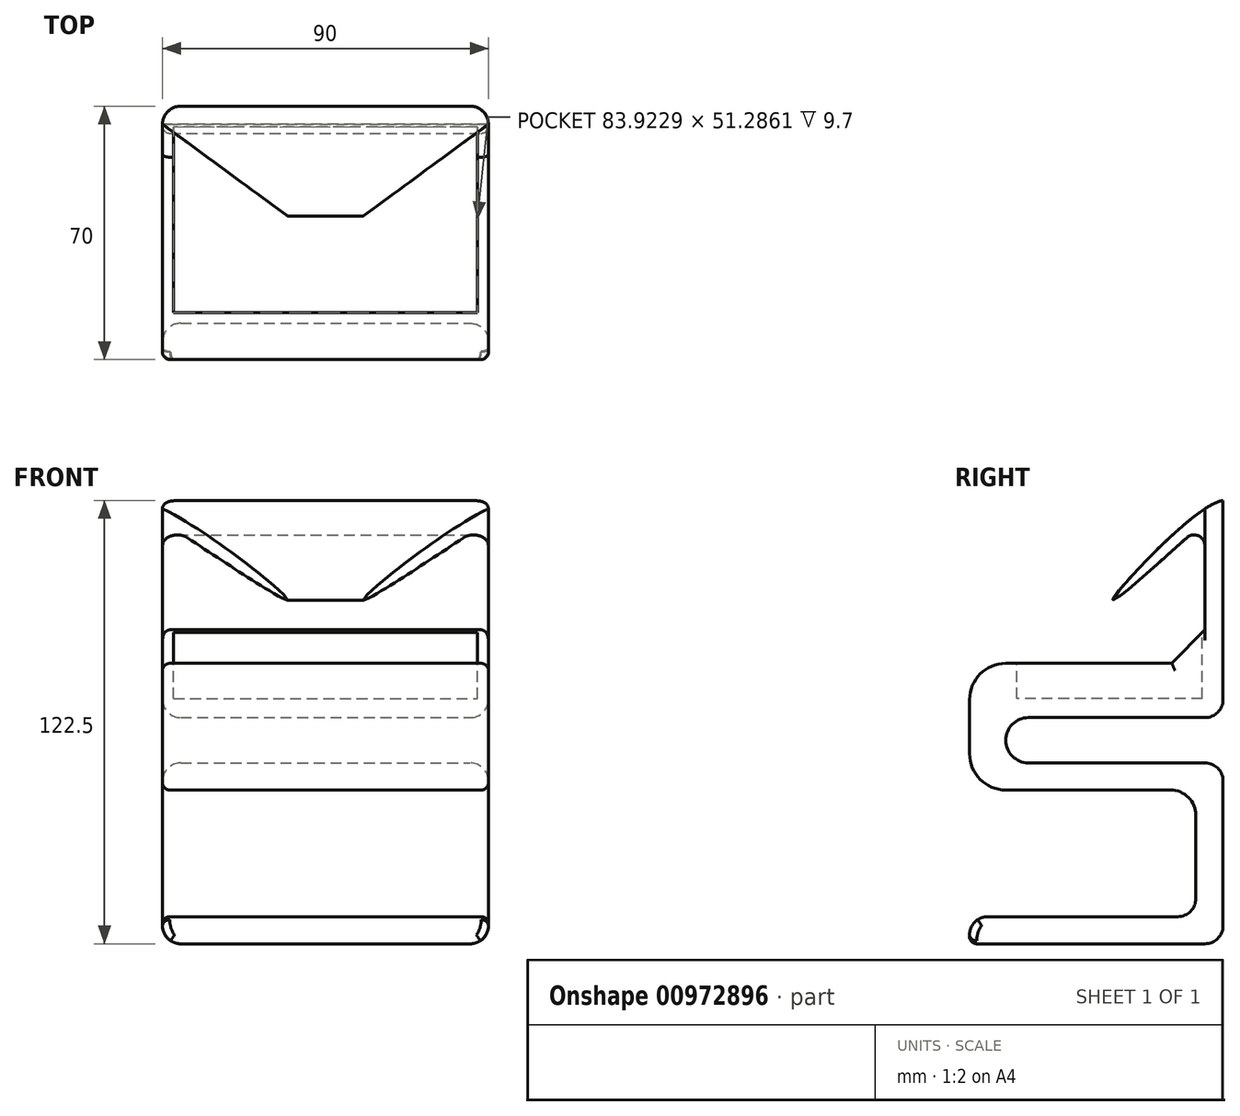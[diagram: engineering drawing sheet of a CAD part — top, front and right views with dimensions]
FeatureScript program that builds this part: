
annotation { "Feature Type Name" : "Feature", "Feature Type Description" : "" }
export const myFeature = defineFeature(function(context is Context, id is Id, definition is map)
    precondition{}
    {
        {
            var Q0;
            Q0=qCreatedBy(makeId("Right.planeOp"),FACE);
            var sketch = newSketch(context, id + "F0", { "sketchPlane" : qUnion([Q0])});
            skLineSegment(sketch, "E0", {"start": v(-39.75, -50) * mm, "end": v(30.25, -50) * mm});
            skLineSegment(sketch, "E1", {"start": v(-39.75, -50) * mm, "end": v(-39.75, -42.5) * mm});
            skLineSegment(sketch, "E2", {"start": v(-39.75, -42.5) * mm, "end": v(22.75, -42.5) * mm});
            skLineSegment(sketch, "E3", {"start": v(30.25, -50) * mm, "end": v(30.25, 0) * mm});
            skLineSegment(sketch, "E4", {"start": v(22.75, -42.5) * mm, "end": v(22.75, -7.5) * mm});
            skLineSegment(sketch, "E5", {"start": v(22.75, -7.5) * mm, "end": v(-39.75, -7.5) * mm});
            skLineSegment(sketch, "E6", {"start": v(-39.75, -7.5) * mm, "end": v(-39.75, 27.5) * mm});
            skLineSegment(sketch, "E7", {"start": v(30.25, 0) * mm, "end": v(-23.5, 0) * mm});
            skArc(sketch, "E8", {"start": v(-23.5, 12.5) * mm, "mid": v(-29.75, 6.25) * mm, "end": v(-23.5, 0) * mm});
            skLineSegment(sketch, "E9", {"start": v(-23.5, 12.5) * mm, "end": v(30.25, 12.5) * mm});
            skLineSegment(sketch, "E10", {"start": v(30.25, 12.5) * mm, "end": v(30.25, 72.5) * mm});
            skLineSegment(sketch, "E11", {"start": v(-39.75, 27.5) * mm, "end": v(16.15, 27.5) * mm});
            skLineSegment(sketch, "E12", {"start": v(16.15, 27.5) * mm, "end": v(25.25, 36.78) * mm});
            skLineSegment(sketch, "E13", {"start": v(25.25, 36.78) * mm, "end": v(25.25, 66.78) * mm});
            skFitSpline(sketch, "E14", {"points": [v(25.25, 66.78) * mm, v(0, 45.52) * mm, v(30.25, 72.5) * mm, v(32.32, 54.21) * mm], "startDerivative": vector(-115.72, -104.64) * mm, "endDerivative": vector(-15.53, -107.77) * mm});
            skSolve(sketch);
        }
        {
            var Q0;
            Q0=makeQuery(id+"F0.imprint","IMPRINT",FACE,{"disambiguationData":[TD([[makeQuery(id+"F0.imprint","IMPRINT",EDGE,{"derivedFrom":sQuery(id+"F0.wireOp",EDGE,"E0")}),1.0]])]});
            extrude(context, id + "F1", {"entities" : qUnion([Q0]), "oppositeDirection" : true, "depth" : 45 * mm, "offsetDistance" : 25 * mm, "hasSecondDirection" : true, "secondDirectionOppositeDirection" : false, "secondDirectionDepth" : 45 * mm});
        }
        {
            var Q0;
            Q0=makeQuery(id+"F1.opExtrude","SWEPT_EDGE",EDGE,{"disambiguationData":[OSD([sQuery(id+"F0.wireOp",EDGE,"E2"),sQuery(id+"F0.wireOp",EDGE,"E4")])]});
            var Q1;
            Q1=makeQuery(id+"F1.opExtrude","SWEPT_EDGE",EDGE,{"disambiguationData":[OSD([sQuery(id+"F0.wireOp",EDGE,"E1"),sQuery(id+"F0.wireOp",EDGE,"E2")])]});
            var Q2;
            Q2=makeQuery(id+"F1.opExtrude","SWEPT_EDGE",EDGE,{"disambiguationData":[OSD([sQuery(id+"F0.wireOp",EDGE,"E3"),sQuery(id+"F0.wireOp",EDGE,"E7")])]});
            var Q3;
            Q3=makeQuery(id+"F1.opExtrude","SWEPT_EDGE",EDGE,{"disambiguationData":[OSD([sQuery(id+"F0.wireOp",EDGE,"E9"),sQuery(id+"F0.wireOp",EDGE,"E10")])]});
            var Q4;
            Q4=makeQuery(id+"F1.opExtrude","SWEPT_EDGE",EDGE,{"disambiguationData":[OSD([sQuery(id+"F0.wireOp",EDGE,"E0"),sQuery(id+"F0.wireOp",EDGE,"E3")])]});
            fillet(context, id + "F2", {"entities" : qUnion([Q0, Q1, Q2, Q3, Q4]), "radius" : 5 * mm, "tangentPropagation" : true, "allowEdgeOverflow" : false});
        }
        {
            var Q0;
            Q0=makeQuery(id+"F1.opExtrude","SWEPT_EDGE",EDGE,{"disambiguationData":[OSD([sQuery(id+"F0.wireOp",EDGE,"E6"),sQuery(id+"F0.wireOp",EDGE,"E11")])]});
            var Q1;
            Q1=makeQuery(id+"F1.opExtrude","SWEPT_EDGE",EDGE,{"disambiguationData":[OSD([sQuery(id+"F0.wireOp",EDGE,"E5"),sQuery(id+"F0.wireOp",EDGE,"E6")])]});
            fillet(context, id + "F3", {"entities" : qUnion([Q0, Q1]), "radius" : 10 * mm, "tangentPropagation" : true, "allowEdgeOverflow" : false});
        }
        {
            var Q0;
            Q0=makeQuery(id+"F1.opExtrude","SWEPT_EDGE",EDGE,{"disambiguationData":[OSD([sQuery(id+"F0.wireOp",EDGE,"E4"),sQuery(id+"F0.wireOp",EDGE,"E5")])]});
            fillet(context, id + "F4", {"entities" : qUnion([Q0]), "radius" : 7 * mm, "tangentPropagation" : true, "allowEdgeOverflow" : false});
        }
        {
            var Q0;
            Q0=qCreatedBy(makeId("Top.planeOp"),FACE);
            cPlane(context, id + "F5", {"entities" : qUnion([Q0]), "cplaneType" : CPlaneType.OFFSET, "offset" : 72.7 * mm, "width" : 150 * mm, "height" : 150 * mm});
        }
        {
            var Q0;
            Q0=qCreatedBy(id+"F5.planeOp",FACE);
            var sketch = newSketch(context, id + "F6", { "sketchPlane" : qUnion([Q0])});
            skLineSegment(sketch, "E15", {"start": v(0, 0) * mm, "end": v(0, 30.25) * mm});
            skLineSegment(sketch, "E16", {"start": v(0, 30.25) * mm, "end": v(-45, 30.25) * mm});
            skLineSegment(sketch, "E17", {"start": v(-45, 30.25) * mm, "end": v(-45, 25.25) * mm});
            skLineSegment(sketch, "E18", {"start": v(0.72, 30.25) * mm, "end": v(45, 30.25) * mm});
            skLineSegment(sketch, "E19", {"start": v(45, 30.25) * mm, "end": v(45, 25.25) * mm});
            skLineSegment(sketch, "E20", {"start": v(0, -0.44) * mm, "end": v(-10, -0.44) * mm});
            skLineSegment(sketch, "E21", {"start": v(-45, 25.25) * mm, "end": v(-10, -0.44) * mm});
            skLineSegment(sketch, "E22", {"start": v(-10, -0.44) * mm, "end": v(-45.04, -0.44) * mm});
            skLineSegment(sketch, "E23", {"start": v(-45, 25.25) * mm, "end": v(-45.04, -0.44) * mm});
            skLineSegment(sketch, "E24.MirrorCS", {"start": v(45, 25.25) * mm, "end": v(45.04, -0.44) * mm});
            skLineSegment(sketch, "E25.MirrorCS", {"start": v(10, -0.44) * mm, "end": v(45.04, -0.44) * mm});
            skLineSegment(sketch, "E26.MirrorCS", {"start": v(45, 25.25) * mm, "end": v(10, -0.44) * mm});
            skSolve(sketch);
        }
        {
            var Q0;
            Q0=makeQuery(id+"F6.imprint","IMPRINT",FACE,{"disambiguationData":[TD([[makeQuery(id+"F6.imprint","IMPRINT",EDGE,{"derivedFrom":sQuery(id+"F6.wireOp",EDGE,"E21")}),-1.0]])]});
            var Q1;
            Q1=makeQuery(id+"F6.imprint","IMPRINT",FACE,{"disambiguationData":[TD([[makeQuery(id+"F6.imprint","IMPRINT",EDGE,{"derivedFrom":sQuery(id+"F6.wireOp",EDGE,"E24.MirrorCS")}),-1.0]])]});
            extrude(context, id + "F7", {"entities" : qUnion([Q0, Q1]), "operationType" : NewBodyOperationType.REMOVE, "oppositeDirection" : true, "depth" : 33.4 * mm, "offsetDistance" : 25 * mm});
        }
        {
            var Q0;
            Q0=makeQuery(id+"F1.opExtrude","SWEPT_EDGE",EDGE,{"disambiguationData":[OSD([sQuery(id+"F0.wireOp",EDGE,"E13"),sQuery(id+"F0.wireOp",EDGE,"E14")])]});
            fillet(context, id + "F8", {"entities" : qUnion([Q0]), "radius" : 3 * mm, "tangentPropagation" : true, "allowEdgeOverflow" : false});
        }
        {
            var Q0;
            Q0=makeQuery(id+"F1.opExtrude","CAP_EDGE",EDGE,{"disambiguationData":[OSD([sQuery(id+"F0.wireOp",EDGE,"E10")])],"isStart":true});
            var Q1;
            Q1=makeQuery(id+"F1.opExtrude","CAP_EDGE",EDGE,{"disambiguationData":[OSD([sQuery(id+"F0.wireOp",EDGE,"E9")])],"isStart":false});
            fillet(context, id + "F9", {"entities" : qUnion([Q0, Q1]), "radius" : 5 * mm, "tangentPropagation" : true, "allowEdgeOverflow" : false});
        }
        {
            var Q0;
            Q0=qCreatedBy(makeId("Top.planeOp"),FACE);
            cPlane(context, id + "F10", {"entities" : qUnion([Q0]), "cplaneType" : CPlaneType.OFFSET, "offset" : 37 * mm, "width" : 150 * mm, "height" : 150 * mm});
        }
        {
            var Q0;
            Q0=qCreatedBy(id+"F10.planeOp",FACE);
            var sketch = newSketch(context, id + "F11", { "sketchPlane" : qUnion([Q0])});
            skPoint(sketch, "E27", {"position": v(-41.96, 24.54) * mm});
            skPoint(sketch, "E28", {"position": v(41.96, 23.4) * mm});
            skLineSegment(sketch, "E29.bottom", {"start": v(-41.96, 24.54) * mm, "end": v(41.96, 24.54) * mm});
            skLineSegment(sketch, "E29.top", {"start": v(-41.96, -26.75) * mm, "end": v(41.96, -26.75) * mm});
            skLineSegment(sketch, "E29.left", {"start": v(-41.96, 24.54) * mm, "end": v(-41.96, -26.75) * mm});
            skLineSegment(sketch, "E29.right", {"start": v(41.96, 24.54) * mm, "end": v(41.96, -26.75) * mm});
            skPoint(sketch, "E30", {"position": v(-41.96, -27.89) * mm});
            skPoint(sketch, "E31", {"position": v(41.96, -27.89) * mm});
            skLineSegment(sketch, "E32.bottom", {"start": v(-41.96, 24.54) * mm, "end": v(38.96, 24.54) * mm});
            skLineSegment(sketch, "E32.top", {"start": v(-41.96, -26.75) * mm, "end": v(38.96, -26.75) * mm});
            skLineSegment(sketch, "E32.right", {"start": v(38.96, 24.54) * mm, "end": v(38.96, -26.75) * mm});
            skSolve(sketch);
        }
        {
            var Q0;
            Q0 = qSketchRegion(id + "F11", true);
            extrude(context, id + "F12", {"entities" : qUnion([Q0]), "operationType" : NewBodyOperationType.REMOVE, "oppositeDirection" : true, "depth" : 19.2 * mm, "offsetDistance" : 25 * mm});
        }
        {
            var Q0;
            Q0=makeQuery(id+"F1.opExtrude","CAP_EDGE",EDGE,{"disambiguationData":[OSD([sQuery(id+"F0.wireOp",EDGE,"E11")])],"isStart":true});
            var Q1;
            Q1=makeQuery(id+"F1.opExtrude","CAP_EDGE",EDGE,{"disambiguationData":[OSD([sQuery(id+"F0.wireOp",EDGE,"E12")])],"isStart":true});
            var Q2;
            Q2=makeQuery(id+"F1.opExtrude","CAP_EDGE",EDGE,{"disambiguationData":[OSD([sQuery(id+"F0.wireOp",EDGE,"E12")])],"isStart":false});
            fillet(context, id + "F13", {"entities" : qUnion([Q0, Q1, Q2]), "radius" : 2 * mm, "tangentPropagation" : true, "allowEdgeOverflow" : false});
        }
    });
